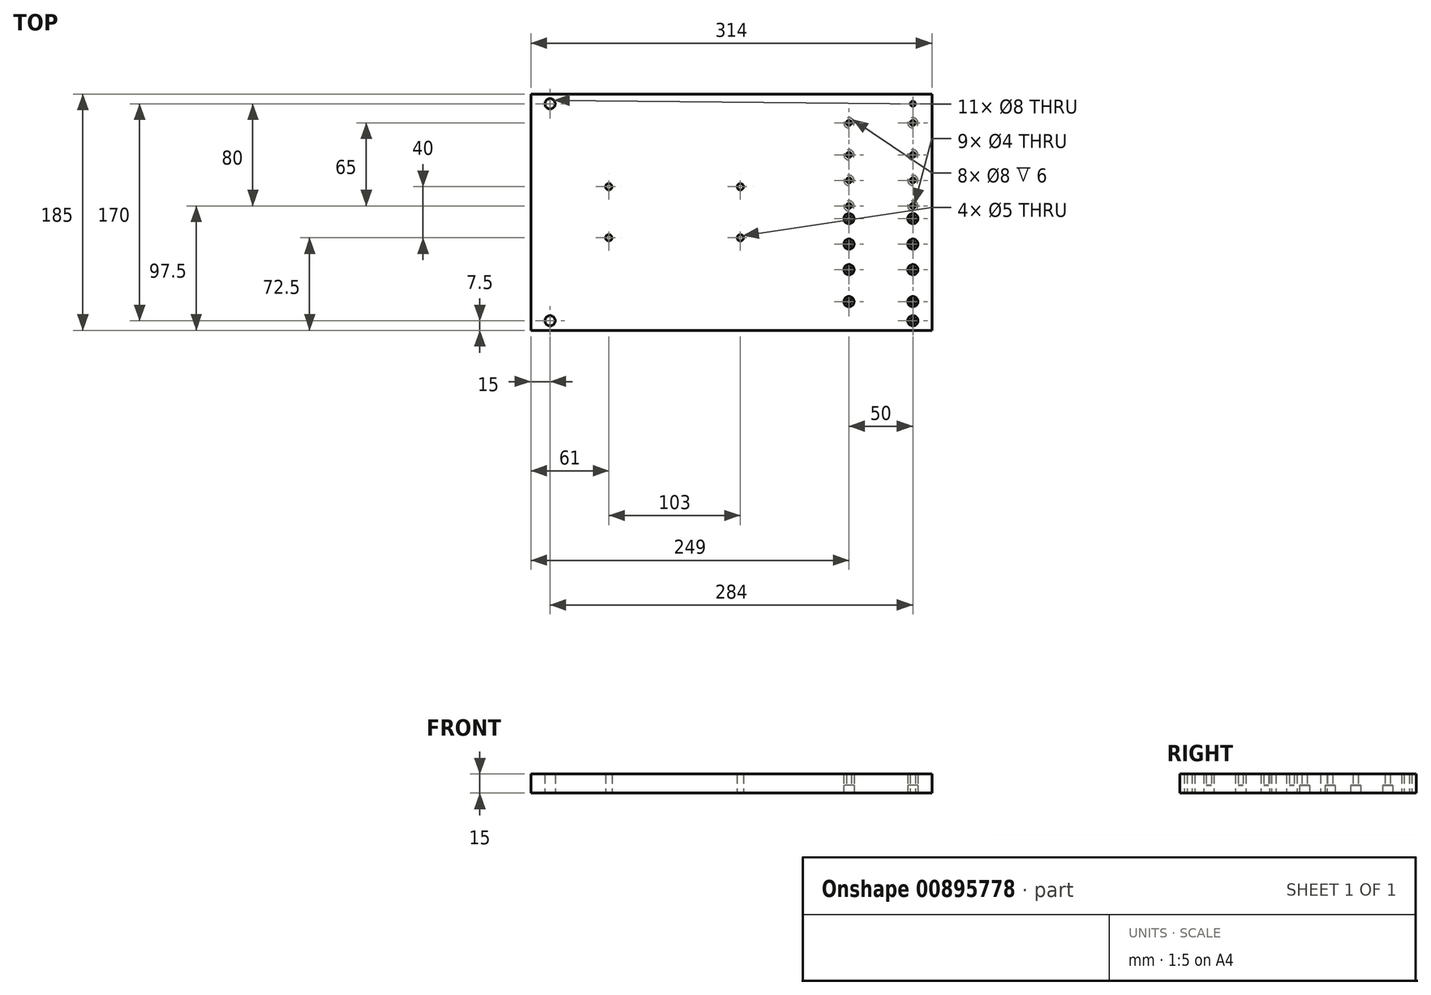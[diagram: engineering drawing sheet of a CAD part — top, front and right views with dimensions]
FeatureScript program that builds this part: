
annotation { "Feature Type Name" : "Feature", "Feature Type Description" : "" }
export const myFeature = defineFeature(function(context is Context, id is Id, definition is map)
    precondition{}
    {
        {
            var Q0;
            Q0=qCreatedBy(makeId("Top.planeOp"),FACE);
            var sketch = newSketch(context, id + "F0", { "sketchPlane" : qUnion([Q0])});
            skLineSegment(sketch, "E0.bottom", {"start": v(-170, 92.5) * mm, "end": v(144, 92.5) * mm});
            skLineSegment(sketch, "E0.top", {"start": v(-170, -92.5) * mm, "end": v(144, -92.5) * mm});
            skLineSegment(sketch, "E0.right", {"start": v(144, 92.5) * mm, "end": v(144, -92.5) * mm});
            skPoint(sketch, "E0.middle", {"position": v(0, 0) * mm});
            skCircle(sketch, "E1", {"center": v(129, 25) * mm, "radius": 2 * mm});
            skCircle(sketch, "E2", {"center": v(79, 25) * mm, "radius": 2 * mm});
            skCircle(sketch, "E3.MirrorC", {"center": v(129, -25) * mm, "radius": 2 * mm});
            skCircle(sketch, "E4.MirrorC", {"center": v(79, -25) * mm, "radius": 2 * mm});
            skCircle(sketch, "E5.0.1.0", {"center": v(79, -5) * mm, "radius": 2 * mm});
            skCircle(sketch, "E5.0.1.1", {"center": v(129, -5) * mm, "radius": 2 * mm});
            skCircle(sketch, "E5.0.1.2", {"center": v(79, 45) * mm, "radius": 2 * mm});
            skCircle(sketch, "E5.0.1.3", {"center": v(129, 45) * mm, "radius": 2 * mm});
            skLineSegment(sketch, "E5.direction1", {"start": v(79, -25) * mm, "end": v(129, -25) * mm, "construction": true});
            skCircle(sketch, "E6.0.1.0", {"center": v(129, 5) * mm, "radius": 2 * mm});
            skCircle(sketch, "E6.0.1.1", {"center": v(79, 5) * mm, "radius": 2 * mm});
            skCircle(sketch, "E6.0.1.2", {"center": v(79, -45) * mm, "radius": 2 * mm});
            skLineSegment(sketch, "E6.0.1.3", {"start": v(79, -45) * mm, "end": v(129, -45) * mm, "construction": true});
            skCircle(sketch, "E6.0.1.4", {"center": v(129, -45) * mm, "radius": 2 * mm});
            skLineSegment(sketch, "E6.direction1", {"start": v(79, 25) * mm, "end": v(79, 25) * mm});
            skLineSegment(sketch, "E7", {"start": v(-170, 92.5) * mm, "end": v(-170, -92.5) * mm});
            skCircle(sketch, "E8.4.0.2", {"center": v(79, -70) * mm, "radius": 2 * mm});
            skLineSegment(sketch, "E8.6.0.2", {"start": v(79, -70) * mm, "end": v(129, -70) * mm, "construction": true});
            skCircle(sketch, "E8.9.0.2", {"center": v(129, -70) * mm, "radius": 2 * mm});
            skCircle(sketch, "E9.4.0.2", {"center": v(79, 70) * mm, "radius": 2 * mm});
            skCircle(sketch, "E9.6.0.2", {"center": v(129, 70) * mm, "radius": 2 * mm});
            skCircle(sketch, "E9.6.0.3", {"center": v(129, 85) * mm, "radius": 2 * mm});
            skCircle(sketch, "E10.9.0.3", {"center": v(129, -85) * mm, "radius": 2 * mm});
            skCircle(sketch, "E11", {"center": v(129, 85) * mm, "radius": 4 * mm});
            skCircle(sketch, "E12", {"center": v(129, 70) * mm, "radius": 4 * mm});
            skCircle(sketch, "E13", {"center": v(79, 70) * mm, "radius": 4 * mm});
            skCircle(sketch, "E14", {"center": v(79, -70) * mm, "radius": 4 * mm});
            skCircle(sketch, "E15", {"center": v(129, -70) * mm, "radius": 4 * mm});
            skCircle(sketch, "E16", {"center": v(129, -85) * mm, "radius": 4 * mm});
            skCircle(sketch, "E17.MirrorC", {"center": v(-155, 85) * mm, "radius": 4 * mm});
            skCircle(sketch, "E18.MirrorC", {"center": v(-155, 85) * mm, "radius": 2 * mm});
            skCircle(sketch, "E19.MirrorC", {"center": v(-155, -85) * mm, "radius": 4 * mm});
            skCircle(sketch, "E20.MirrorC", {"center": v(-155, -85) * mm, "radius": 2 * mm});
            skCircle(sketch, "E21", {"center": v(-109, 20) * mm, "radius": 2.5 * mm});
            skCircle(sketch, "E22", {"center": v(-6, 20) * mm, "radius": 2.5 * mm});
            skCircle(sketch, "E23", {"center": v(-6, -20) * mm, "radius": 2.5 * mm});
            skCircle(sketch, "E24", {"center": v(-109, -20) * mm, "radius": 2.5 * mm});
            skCircle(sketch, "E25", {"center": v(79, 45) * mm, "radius": 4 * mm});
            skCircle(sketch, "E26", {"center": v(129, 45) * mm, "radius": 4 * mm});
            skCircle(sketch, "E27", {"center": v(79, 25) * mm, "radius": 4 * mm});
            skCircle(sketch, "E28", {"center": v(129, 25) * mm, "radius": 4 * mm});
            skCircle(sketch, "E29", {"center": v(79, 5) * mm, "radius": 4 * mm});
            skCircle(sketch, "E30", {"center": v(79, -25) * mm, "radius": 4 * mm});
            skCircle(sketch, "E31", {"center": v(79, -45) * mm, "radius": 4 * mm});
            skCircle(sketch, "E32", {"center": v(129, -45) * mm, "radius": 4 * mm});
            skCircle(sketch, "E33", {"center": v(129, -25) * mm, "radius": 4 * mm});
            skCircle(sketch, "E34", {"center": v(129, -5) * mm, "radius": 4 * mm});
            skCircle(sketch, "E35", {"center": v(129, 5) * mm, "radius": 4 * mm});
            skCircle(sketch, "E36", {"center": v(79, -5) * mm, "radius": 4 * mm});
            skSolve(sketch);
        }
        {
            var Q0;
            Q0=makeQuery(id+"F0.imprint","IMPRINT",FACE,{"disambiguationData":[TD([[makeQuery(id+"F0.imprint","IMPRINT",EDGE,{"derivedFrom":sQuery(id+"F0.wireOp",EDGE,"E0.bottom")}),-1.0]])]});
            var Q1;
            Q1=makeQuery(id+"F0.imprint","IMPRINT",FACE,{"disambiguationData":[TD([[makeQuery(id+"F0.imprint","IMPRINT",EDGE,{"derivedFrom":sQuery(id+"F0.wireOp",EDGE,"tP1cKA6P-DnEm-xsQW-bf5u-ro4NOA7zcUQ0")}),-1.0]])]});
            var Q2;
            Q2=makeQuery(id+"F0.imprint","IMPRINT",FACE,{"disambiguationData":[TD([[makeQuery(id+"F0.imprint","IMPRINT",EDGE,{"derivedFrom":sQuery(id+"F0.wireOp",EDGE,"KS7B0Tgv-yC0R-UZgO-3D7h-MfusDyucgrnt")}),-1.0]])]});
            var Q3;
            Q3=makeQuery(id+"F0.imprint","IMPRINT",FACE,{"disambiguationData":[TD([[makeQuery(id+"F0.imprint","IMPRINT",EDGE,{"derivedFrom":sQuery(id+"F0.wireOp",EDGE,"GhH9Vfsf-wevH-dspP-nIH1-JVybMqvmfzty")}),-1.0]])]});
            var Q4;
            Q4=makeQuery(id+"F0.imprint","IMPRINT",FACE,{"disambiguationData":[TD([[makeQuery(id+"F0.imprint","IMPRINT",EDGE,{"derivedFrom":sQuery(id+"F0.wireOp",EDGE,"5kgpbS65-8kDK-6VSx-XlGb-DQDUuwFPtWOm")}),-1.0]])]});
            var Q5;
            Q5=makeQuery(id+"F0.imprint","IMPRINT",FACE,{"disambiguationData":[TD([[makeQuery(id+"F0.imprint","IMPRINT",EDGE,{"derivedFrom":sQuery(id+"F0.wireOp",EDGE,"s2GrKOWq-Te8Q-NBOx-DEZZ-G3uV5kvdJo70")}),-1.0]])]});
            var Q6;
            Q6=makeQuery(id+"F0.imprint","IMPRINT",FACE,{"disambiguationData":[TD([[makeQuery(id+"F0.imprint","IMPRINT",EDGE,{"derivedFrom":sQuery(id+"F0.wireOp",EDGE,"IOOrEQ0n-cQHP-w6Xy-iuh4-GMHoJjsOReun")}),-1.0]])]});
            var Q7;
            Q7=makeQuery(id+"F0.imprint","IMPRINT",FACE,{"disambiguationData":[TD([[makeQuery(id+"F0.imprint","IMPRINT",EDGE,{"derivedFrom":sQuery(id+"F0.wireOp",EDGE,"Mz5kEJI8-WlXS-lr4h-mN2i-G7SbCAZtr9Pr")}),-1.0]])]});
            var Q8;
            Q8=makeQuery(id+"F0.imprint","IMPRINT",FACE,{"disambiguationData":[TD([[makeQuery(id+"F0.imprint","IMPRINT",EDGE,{"derivedFrom":sQuery(id+"F0.wireOp",EDGE,"QboWkG7Q-UUmW-YJw4-jwft-uvQwTnENFoAH")}),-1.0]])]});
            var Q9;
            Q9=makeQuery(id+"F0.imprint","IMPRINT",FACE,{"disambiguationData":[TD([[makeQuery(id+"F0.imprint","IMPRINT",EDGE,{"derivedFrom":sQuery(id+"F0.wireOp",EDGE,"L3sS62ht-eBsq-3WIz-wQ5J-nAW7e2QGFpIA")}),-1.0]])]});
            var Q10;
            Q10=makeQuery(id+"F0.imprint","IMPRINT",FACE,{"disambiguationData":[TD([[makeQuery(id+"F0.imprint","IMPRINT",EDGE,{"derivedFrom":sQuery(id+"F0.wireOp",EDGE,"E2")}),-1.0]])]});
            var Q11;
            Q11=makeQuery(id+"F0.imprint","IMPRINT",FACE,{"disambiguationData":[TD([[makeQuery(id+"F0.imprint","IMPRINT",EDGE,{"derivedFrom":sQuery(id+"F0.wireOp",EDGE,"E8.4.0.2")}),1.0]])]});
            var Q12;
            Q12=makeQuery(id+"F0.imprint","IMPRINT",FACE,{"disambiguationData":[TD([[makeQuery(id+"F0.imprint","IMPRINT",EDGE,{"derivedFrom":sQuery(id+"F0.wireOp",EDGE,"E8.9.0.2")}),1.0]])]});
            var Q13;
            Q13=makeQuery(id+"F0.imprint","IMPRINT",FACE,{"disambiguationData":[TD([[makeQuery(id+"F0.imprint","IMPRINT",EDGE,{"derivedFrom":sQuery(id+"F0.wireOp",EDGE,"E10.4.0.3")}),1.0]])]});
            var Q14;
            Q14=makeQuery(id+"F0.imprint","IMPRINT",FACE,{"disambiguationData":[TD([[makeQuery(id+"F0.imprint","IMPRINT",EDGE,{"derivedFrom":sQuery(id+"F0.wireOp",EDGE,"E10.9.0.3")}),1.0]])]});
            var Q15;
            Q15=makeQuery(id+"F0.imprint","IMPRINT",FACE,{"disambiguationData":[TD([[makeQuery(id+"F0.imprint","IMPRINT",EDGE,{"derivedFrom":sQuery(id+"F0.wireOp",EDGE,"E9.6.0.3")}),-1.0]])]});
            var Q16;
            Q16=makeQuery(id+"F0.imprint","IMPRINT",FACE,{"disambiguationData":[TD([[makeQuery(id+"F0.imprint","IMPRINT",EDGE,{"derivedFrom":sQuery(id+"F0.wireOp",EDGE,"E9.6.0.2")}),-1.0]])]});
            var Q17;
            Q17=makeQuery(id+"F0.imprint","IMPRINT",FACE,{"disambiguationData":[TD([[makeQuery(id+"F0.imprint","IMPRINT",EDGE,{"derivedFrom":sQuery(id+"F0.wireOp",EDGE,"E1")}),-1.0]])]});
            var Q18;
            Q18=makeQuery(id+"F0.imprint","IMPRINT",FACE,{"disambiguationData":[TD([[makeQuery(id+"F0.imprint","IMPRINT",EDGE,{"derivedFrom":sQuery(id+"F0.wireOp",EDGE,"E9.4.0.2")}),-1.0]])]});
            var Q19;
            Q19=makeQuery(id+"F0.imprint","IMPRINT",FACE,{"disambiguationData":[TD([[makeQuery(id+"F0.imprint","IMPRINT",EDGE,{"derivedFrom":sQuery(id+"F0.wireOp",EDGE,"E9.4.0.3")}),-1.0]])]});
            var Q20;
            Q20=makeQuery(id+"F0.imprint","IMPRINT",FACE,{"disambiguationData":[TD([[makeQuery(id+"F0.imprint","IMPRINT",EDGE,{"derivedFrom":sQuery(id+"F0.wireOp",EDGE,"E17.MirrorC")}),-1.0]])]});
            var Q21;
            Q21=makeQuery(id+"F0.imprint","IMPRINT",FACE,{"disambiguationData":[TD([[makeQuery(id+"F0.imprint","IMPRINT",EDGE,{"derivedFrom":sQuery(id+"F0.wireOp",EDGE,"E19.MirrorC")}),-1.0]])]});
            var Q22;
            Q22=makeQuery(id+"F0.imprint","IMPRINT",FACE,{"disambiguationData":[TD([[makeQuery(id+"F0.imprint","IMPRINT",EDGE,{"derivedFrom":sQuery(id+"F0.wireOp",EDGE,"E5.0.1.2")}),-1.0]])]});
            var Q23;
            Q23=makeQuery(id+"F0.imprint","IMPRINT",FACE,{"disambiguationData":[TD([[makeQuery(id+"F0.imprint","IMPRINT",EDGE,{"derivedFrom":sQuery(id+"F0.wireOp",EDGE,"E6.0.1.1")}),-1.0]])]});
            var Q24;
            Q24=makeQuery(id+"F0.imprint","IMPRINT",FACE,{"disambiguationData":[TD([[makeQuery(id+"F0.imprint","IMPRINT",EDGE,{"derivedFrom":sQuery(id+"F0.wireOp",EDGE,"E5.0.1.0")}),1.0]])]});
            var Q25;
            Q25=makeQuery(id+"F0.imprint","IMPRINT",FACE,{"disambiguationData":[TD([[makeQuery(id+"F0.imprint","IMPRINT",EDGE,{"derivedFrom":sQuery(id+"F0.wireOp",EDGE,"E4.MirrorC")}),1.0]])]});
            var Q26;
            Q26=makeQuery(id+"F0.imprint","IMPRINT",FACE,{"disambiguationData":[TD([[makeQuery(id+"F0.imprint","IMPRINT",EDGE,{"derivedFrom":sQuery(id+"F0.wireOp",EDGE,"E6.0.1.2")}),1.0]])]});
            var Q27;
            Q27=makeQuery(id+"F0.imprint","IMPRINT",FACE,{"disambiguationData":[TD([[makeQuery(id+"F0.imprint","IMPRINT",EDGE,{"derivedFrom":sQuery(id+"F0.wireOp",EDGE,"E6.0.1.4")}),1.0]])]});
            var Q28;
            Q28=makeQuery(id+"F0.imprint","IMPRINT",FACE,{"disambiguationData":[TD([[makeQuery(id+"F0.imprint","IMPRINT",EDGE,{"derivedFrom":sQuery(id+"F0.wireOp",EDGE,"E3.MirrorC")}),1.0]])]});
            var Q29;
            Q29=makeQuery(id+"F0.imprint","IMPRINT",FACE,{"disambiguationData":[TD([[makeQuery(id+"F0.imprint","IMPRINT",EDGE,{"derivedFrom":sQuery(id+"F0.wireOp",EDGE,"E5.0.1.1")}),1.0]])]});
            var Q30;
            Q30=makeQuery(id+"F0.imprint","IMPRINT",FACE,{"disambiguationData":[TD([[makeQuery(id+"F0.imprint","IMPRINT",EDGE,{"derivedFrom":sQuery(id+"F0.wireOp",EDGE,"E6.0.1.0")}),-1.0]])]});
            var Q31;
            Q31=makeQuery(id+"F0.imprint","IMPRINT",FACE,{"disambiguationData":[TD([[makeQuery(id+"F0.imprint","IMPRINT",EDGE,{"derivedFrom":sQuery(id+"F0.wireOp",EDGE,"E5.0.1.3")}),-1.0]])]});
            extrude(context, id + "F1", {"entities" : qUnion([Q0, Q1, Q2, Q3, Q4, Q5, Q6, Q7, Q8, Q9, Q10, Q11, Q12, Q13, Q14, Q15, Q16, Q17, Q18, Q19, Q20, Q21, Q22, Q23, Q24, Q25, Q26, Q27, Q28, Q29, Q30, Q31]), "depth" : 15 * mm, "offsetDistance" : 25 * mm});
        }
        {
            var Q0;
            Q0=makeQuery(id+"F0.imprint","IMPRINT",FACE,{"disambiguationData":[TD([[makeQuery(id+"F0.imprint","IMPRINT",EDGE,{"derivedFrom":sQuery(id+"F0.wireOp",EDGE,"tP1cKA6P-DnEm-xsQW-bf5u-ro4NOA7zcUQ0")}),-1.0]])]});
            var Q1;
            Q1=makeQuery(id+"F0.imprint","IMPRINT",FACE,{"disambiguationData":[TD([[makeQuery(id+"F0.imprint","IMPRINT",EDGE,{"derivedFrom":sQuery(id+"F0.wireOp",EDGE,"Mz5kEJI8-WlXS-lr4h-mN2i-G7SbCAZtr9Pr")}),-1.0]])]});
            var Q2;
            Q2=makeQuery(id+"F0.imprint","IMPRINT",FACE,{"disambiguationData":[TD([[makeQuery(id+"F0.imprint","IMPRINT",EDGE,{"derivedFrom":sQuery(id+"F0.wireOp",EDGE,"L3sS62ht-eBsq-3WIz-wQ5J-nAW7e2QGFpIA")}),-1.0]])]});
            var Q3;
            Q3=makeQuery(id+"F0.imprint","IMPRINT",FACE,{"disambiguationData":[TD([[makeQuery(id+"F0.imprint","IMPRINT",EDGE,{"derivedFrom":sQuery(id+"F0.wireOp",EDGE,"QboWkG7Q-UUmW-YJw4-jwft-uvQwTnENFoAH")}),-1.0]])]});
            var Q4;
            Q4=makeQuery(id+"F0.imprint","IMPRINT",FACE,{"disambiguationData":[TD([[makeQuery(id+"F0.imprint","IMPRINT",EDGE,{"derivedFrom":sQuery(id+"F0.wireOp",EDGE,"IOOrEQ0n-cQHP-w6Xy-iuh4-GMHoJjsOReun")}),-1.0]])]});
            var Q5;
            Q5=makeQuery(id+"F0.imprint","IMPRINT",FACE,{"disambiguationData":[TD([[makeQuery(id+"F0.imprint","IMPRINT",EDGE,{"derivedFrom":sQuery(id+"F0.wireOp",EDGE,"KS7B0Tgv-yC0R-UZgO-3D7h-MfusDyucgrnt")}),-1.0]])]});
            var Q6;
            Q6=makeQuery(id+"F0.imprint","IMPRINT",FACE,{"disambiguationData":[TD([[makeQuery(id+"F0.imprint","IMPRINT",EDGE,{"derivedFrom":sQuery(id+"F0.wireOp",EDGE,"5kgpbS65-8kDK-6VSx-XlGb-DQDUuwFPtWOm")}),-1.0]])]});
            var Q7;
            Q7=makeQuery(id+"F0.imprint","IMPRINT",FACE,{"disambiguationData":[TD([[makeQuery(id+"F0.imprint","IMPRINT",EDGE,{"derivedFrom":sQuery(id+"F0.wireOp",EDGE,"s2GrKOWq-Te8Q-NBOx-DEZZ-G3uV5kvdJo70")}),-1.0]])]});
            var Q8;
            Q8=makeQuery(id+"F0.imprint","IMPRINT",FACE,{"disambiguationData":[TD([[makeQuery(id+"F0.imprint","IMPRINT",EDGE,{"derivedFrom":sQuery(id+"F0.wireOp",EDGE,"GhH9Vfsf-wevH-dspP-nIH1-JVybMqvmfzty")}),-1.0]])]});
            var Q9;
            Q9=makeQuery(id+"F0.imprint","IMPRINT",FACE,{"disambiguationData":[TD([[makeQuery(id+"F0.imprint","IMPRINT",EDGE,{"derivedFrom":sQuery(id+"F0.wireOp",EDGE,"E2")}),-1.0]])]});
            var Q10;
            Q10=makeQuery(id+"F0.imprint","IMPRINT",FACE,{"disambiguationData":[TD([[makeQuery(id+"F0.imprint","IMPRINT",EDGE,{"derivedFrom":sQuery(id+"F0.wireOp",EDGE,"E1")}),-1.0]])]});
            var Q11;
            Q11=makeQuery(id+"F0.imprint","IMPRINT",FACE,{"disambiguationData":[TD([[makeQuery(id+"F0.imprint","IMPRINT",EDGE,{"derivedFrom":sQuery(id+"F0.wireOp",EDGE,"E9.4.0.3")}),-1.0]])]});
            var Q12;
            Q12=makeQuery(id+"F0.imprint","IMPRINT",FACE,{"disambiguationData":[TD([[makeQuery(id+"F0.imprint","IMPRINT",EDGE,{"derivedFrom":sQuery(id+"F0.wireOp",EDGE,"E9.6.0.2")}),-1.0]])]});
            var Q13;
            Q13=makeQuery(id+"F0.imprint","IMPRINT",FACE,{"disambiguationData":[TD([[makeQuery(id+"F0.imprint","IMPRINT",EDGE,{"derivedFrom":sQuery(id+"F0.wireOp",EDGE,"E9.4.0.2")}),-1.0]])]});
            var Q14;
            Q14=makeQuery(id+"F0.imprint","IMPRINT",FACE,{"disambiguationData":[TD([[makeQuery(id+"F0.imprint","IMPRINT",EDGE,{"derivedFrom":sQuery(id+"F0.wireOp",EDGE,"E8.4.0.2")}),1.0]])]});
            var Q15;
            Q15=makeQuery(id+"F0.imprint","IMPRINT",FACE,{"disambiguationData":[TD([[makeQuery(id+"F0.imprint","IMPRINT",EDGE,{"derivedFrom":sQuery(id+"F0.wireOp",EDGE,"E8.9.0.2")}),1.0]])]});
            var Q16;
            Q16=makeQuery(id+"F0.imprint","IMPRINT",FACE,{"disambiguationData":[TD([[makeQuery(id+"F0.imprint","IMPRINT",EDGE,{"derivedFrom":sQuery(id+"F0.wireOp",EDGE,"E10.4.0.3")}),1.0]])]});
            var Q17;
            Q17=makeQuery(id+"F0.imprint","IMPRINT",FACE,{"disambiguationData":[TD([[makeQuery(id+"F0.imprint","IMPRINT",EDGE,{"derivedFrom":sQuery(id+"F0.wireOp",EDGE,"E5.0.1.2")}),-1.0]])]});
            var Q18;
            Q18=makeQuery(id+"F0.imprint","IMPRINT",FACE,{"disambiguationData":[TD([[makeQuery(id+"F0.imprint","IMPRINT",EDGE,{"derivedFrom":sQuery(id+"F0.wireOp",EDGE,"E5.0.1.3")}),-1.0]])]});
            var Q19;
            Q19=makeQuery(id+"F0.imprint","IMPRINT",FACE,{"disambiguationData":[TD([[makeQuery(id+"F0.imprint","IMPRINT",EDGE,{"derivedFrom":sQuery(id+"F0.wireOp",EDGE,"E6.0.1.0")}),-1.0]])]});
            var Q20;
            Q20=makeQuery(id+"F0.imprint","IMPRINT",FACE,{"disambiguationData":[TD([[makeQuery(id+"F0.imprint","IMPRINT",EDGE,{"derivedFrom":sQuery(id+"F0.wireOp",EDGE,"E5.0.1.1")}),1.0]])]});
            var Q21;
            Q21=makeQuery(id+"F0.imprint","IMPRINT",FACE,{"disambiguationData":[TD([[makeQuery(id+"F0.imprint","IMPRINT",EDGE,{"derivedFrom":sQuery(id+"F0.wireOp",EDGE,"E3.MirrorC")}),1.0]])]});
            var Q22;
            Q22=makeQuery(id+"F0.imprint","IMPRINT",FACE,{"disambiguationData":[TD([[makeQuery(id+"F0.imprint","IMPRINT",EDGE,{"derivedFrom":sQuery(id+"F0.wireOp",EDGE,"E6.0.1.4")}),1.0]])]});
            var Q23;
            Q23=makeQuery(id+"F0.imprint","IMPRINT",FACE,{"disambiguationData":[TD([[makeQuery(id+"F0.imprint","IMPRINT",EDGE,{"derivedFrom":sQuery(id+"F0.wireOp",EDGE,"E6.0.1.2")}),1.0]])]});
            var Q24;
            Q24=makeQuery(id+"F0.imprint","IMPRINT",FACE,{"disambiguationData":[TD([[makeQuery(id+"F0.imprint","IMPRINT",EDGE,{"derivedFrom":sQuery(id+"F0.wireOp",EDGE,"E4.MirrorC")}),1.0]])]});
            var Q25;
            Q25=makeQuery(id+"F0.imprint","IMPRINT",FACE,{"disambiguationData":[TD([[makeQuery(id+"F0.imprint","IMPRINT",EDGE,{"derivedFrom":sQuery(id+"F0.wireOp",EDGE,"E5.0.1.0")}),1.0]])]});
            var Q26;
            Q26=makeQuery(id+"F0.imprint","IMPRINT",FACE,{"disambiguationData":[TD([[makeQuery(id+"F0.imprint","IMPRINT",EDGE,{"derivedFrom":sQuery(id+"F0.wireOp",EDGE,"E6.0.1.1")}),-1.0]])]});
            extrude(context, id + "F2", {"entities" : qUnion([Q0, Q1, Q2, Q3, Q4, Q5, Q6, Q7, Q8, Q9, Q10, Q11, Q12, Q13, Q14, Q15, Q16, Q17, Q18, Q19, Q20, Q21, Q22, Q23, Q24, Q25, Q26]), "operationType" : NewBodyOperationType.REMOVE, "depth" : 6 * mm, "offsetDistance" : 25 * mm});
        }
    });
